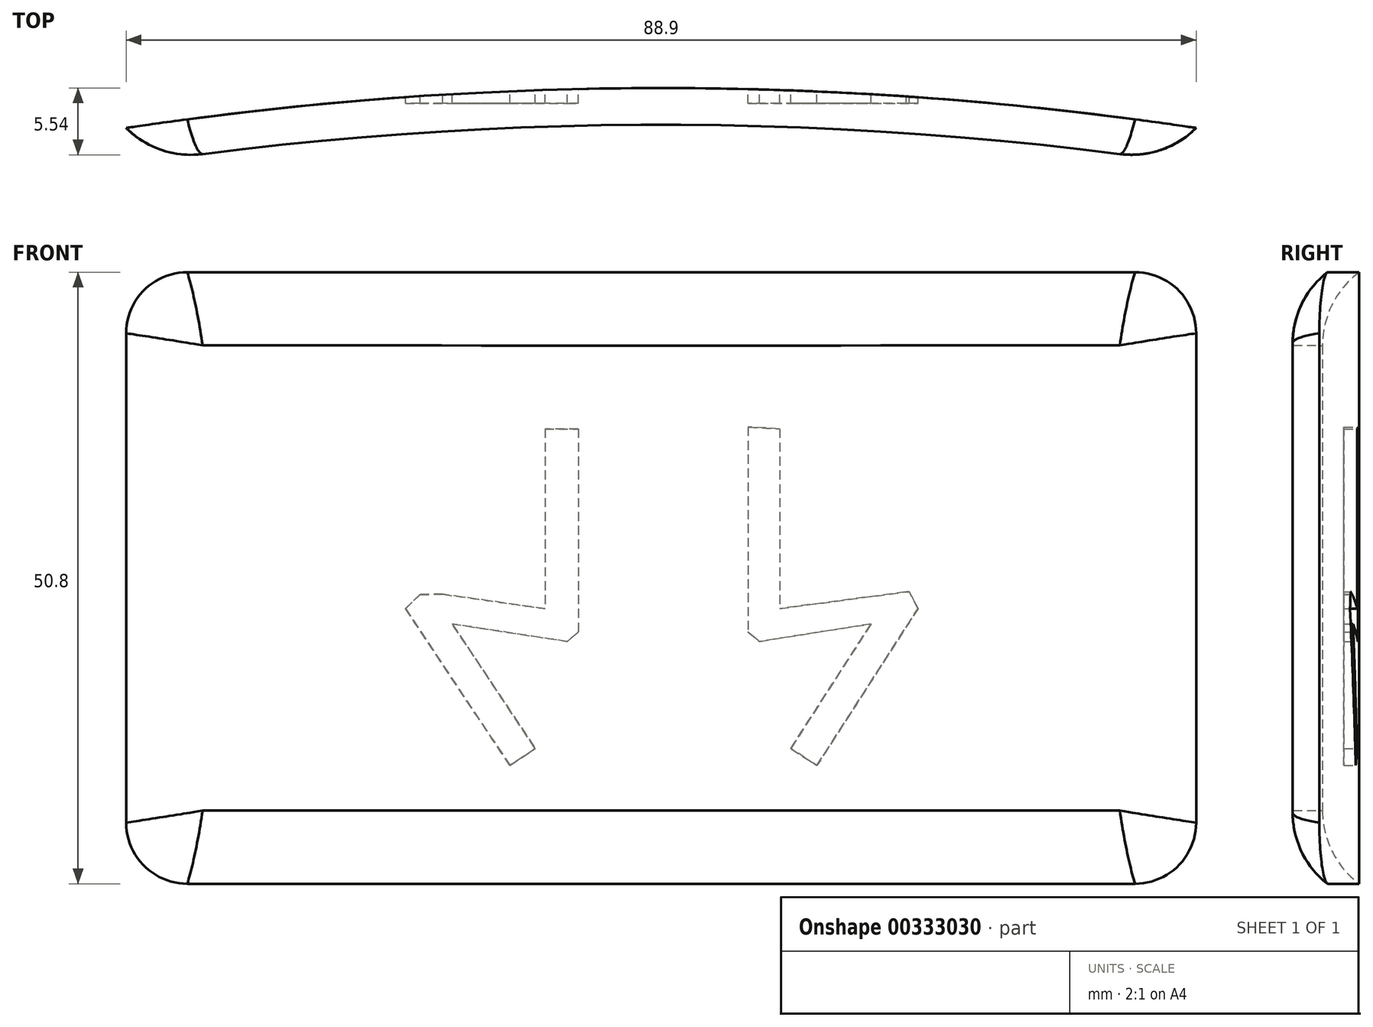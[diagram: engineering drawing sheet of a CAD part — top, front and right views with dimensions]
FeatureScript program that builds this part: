
annotation { "Feature Type Name" : "Feature", "Feature Type Description" : "" }
export const myFeature = defineFeature(function(context is Context, id is Id, definition is map)
    precondition{}
    {
        {
            var Q0;
            Q0=qCreatedBy(makeId("Top.planeOp"),FACE);
            var sketch = newSketch(context, id + "F0", { "sketchPlane" : qUnion([Q0])});
            skLineSegment(sketch, "E0", {"start": v(-42.15, 0) * mm, "end": v(-42.15, 3.05) * mm});
            skLineSegment(sketch, "E1", {"start": v(46.75, 0) * mm, "end": v(46.75, 3.05) * mm});
            skArc(sketch, "E2", {"start": v(46.75, 3.05) * mm, "mid": v(2.3, 6.36) * mm, "end": v(-42.15, 3.05) * mm});
            skArc(sketch, "E3", {"start": v(46.75, 0) * mm, "mid": v(2.3, 3.31) * mm, "end": v(-42.15, 0) * mm});
            skSolve(sketch);
        }
        {
            var Q0;
            Q0 = qSketchRegion(id + "F0", true);
            extrude(context, id + "F1", {"entities" : qUnion([Q0]), "depth" : 50.8 * mm});
        }
        {
            var Q0;
            Q0=makeQuery(id+"F1.opExtrude","CAP_EDGE",EDGE,{"disambiguationData":[OSD([sQuery(id+"F0.wireOp",EDGE,"E0")])],"isStart":true});
            var Q1;
            Q1=makeQuery(id+"F1.opExtrude","CAP_EDGE",EDGE,{"disambiguationData":[OSD([sQuery(id+"F0.wireOp",EDGE,"E1")])],"isStart":true});
            var Q2;
            Q2=makeQuery(id+"F1.opExtrude","CAP_EDGE",EDGE,{"disambiguationData":[OSD([sQuery(id+"F0.wireOp",EDGE,"E1")])],"isStart":false});
            var Q3;
            Q3=makeQuery(id+"F1.opExtrude","CAP_EDGE",EDGE,{"disambiguationData":[OSD([sQuery(id+"F0.wireOp",EDGE,"E0")])],"isStart":false});
            fillet(context, id + "F2", {"entities" : qUnion([Q0, Q1, Q2, Q3]), "radius" : 5.08 * mm, "tangentPropagation" : true, "allowEdgeOverflow" : false});
        }
        {
            var Q0;
            Q0=makeQuery(id+"F1.opExtrude","SWEPT_FACE",FACE,{"disambiguationData":[OSD([sQuery(id+"F0.wireOp",EDGE,"ed1f61be-c009-4c42-bc88-0e2171d65392")])]});
            var Q1;
            Q1=makeQuery(id+"F1.opExtrude","SWEPT_FACE",FACE,{"disambiguationData":[OSD([sQuery(id+"F0.wireOp",EDGE,"E3")])]});
            fillet(context, id + "F3", {"entities" : qUnion([Q0, Q1]), "radius" : 7.62 * mm, "tangentPropagation" : true, "allowEdgeOverflow" : false});
        }
        {
            var Q0;
            Q0=qCreatedBy(makeId("Front.planeOp"),FACE);
            cPlane(context, id + "F4", {"entities" : qUnion([Q0]), "cplaneType" : CPlaneType.OFFSET, "offset" : 7.62 * mm, "oppositeDirection" : true, "width" : 152.4 * mm, "height" : 152.4 * mm});
        }
        {
            var Q0;
            Q0=qCreatedBy(id+"F4.planeOp",FACE);
            var sketch = newSketch(context, id + "F5", { "sketchPlane" : qUnion([Q0])});
            skPoint(sketch, "E4.startSnap0", {"position": v(25.93, 24) * mm});
            skLineSegment(sketch, "E5", {"start": v(9.53, 37.94) * mm, "end": v(9.53, 20.9) * mm});
            skLineSegment(sketch, "E6", {"start": v(9.53, 20.9) * mm, "end": v(10.45, 20.13) * mm});
            skLineSegment(sketch, "E7", {"start": v(10.45, 20.13) * mm, "end": v(19.74, 21.59) * mm});
            skLineSegment(sketch, "E8", {"start": v(19.74, 21.59) * mm, "end": v(13.06, 11.23) * mm});
            skLineSegment(sketch, "E9", {"start": v(13.06, 11.23) * mm, "end": v(15.24, 9.82) * mm});
            skLineSegment(sketch, "E10", {"start": v(15.24, 9.82) * mm, "end": v(23.63, 22.85) * mm});
            skLineSegment(sketch, "E11", {"start": v(23.63, 22.85) * mm, "end": v(22.88, 24.27) * mm});
            skLineSegment(sketch, "E12", {"start": v(22.88, 24.27) * mm, "end": v(12.14, 22.85) * mm});
            skLineSegment(sketch, "E13", {"start": v(12.14, 22.85) * mm, "end": v(12.14, 37.78) * mm});
            skLineSegment(sketch, "E14", {"start": v(12.14, 37.78) * mm, "end": v(9.53, 37.94) * mm});
            skLineSegment(sketch, "E15", {"start": v(-4.6, 37.78) * mm, "end": v(-7.36, 37.78) * mm});
            skLineSegment(sketch, "E16", {"start": v(-7.36, 37.78) * mm, "end": v(-7.36, 22.85) * mm});
            skLineSegment(sketch, "E17", {"start": v(-7.36, 22.85) * mm, "end": v(-17.49, 24.27) * mm});
            skLineSegment(sketch, "E18", {"start": v(-17.49, 24.27) * mm, "end": v(-18.94, 22.85) * mm});
            skLineSegment(sketch, "E19", {"start": v(-18.94, 22.85) * mm, "end": v(-10.27, 9.82) * mm});
            skLineSegment(sketch, "E20", {"start": v(-10.27, 9.82) * mm, "end": v(-8.16, 11.23) * mm});
            skLineSegment(sketch, "E21", {"start": v(-8.16, 11.23) * mm, "end": v(-15.06, 21.59) * mm});
            skLineSegment(sketch, "E22", {"start": v(-15.06, 21.59) * mm, "end": v(-5.51, 20.13) * mm});
            skLineSegment(sketch, "E23", {"start": v(-5.51, 20.13) * mm, "end": v(-4.6, 20.9) * mm});
            skLineSegment(sketch, "E24", {"start": v(-4.6, 20.9) * mm, "end": v(-4.6, 37.78) * mm});
            skLineSegment(sketch, "E25", {"start": v(22.9, 24.25) * mm, "end": v(22.65, 24.24) * mm});
            skPoint(sketch, "E25.endSnap0", {"position": v(-21.25, 24) * mm});
            skLineSegment(sketch, "E26", {"start": v(28.56, 22.85) * mm, "end": v(28.56, 24.27) * mm});
            skPoint(sketch, "E27.end.orphan", {"position": v(-24.09, 22.85) * mm});
            skPoint(sketch, "E27.start.orphan", {"position": v(-24.09, 24) * mm});
            skLineSegment(sketch, "E28.trimOffspring", {"start": v(-15.85, 24.04) * mm, "end": v(-17.73, 24.03) * mm});
            skSolve(sketch);
        }
        {
            var Q0;
            Q0=makeQuery(id+"F5.imprint","IMPRINT",FACE,{"disambiguationData":[TD([[makeQuery(id+"F5.imprint","IMPRINT",EDGE,{"derivedFrom":sQuery(id+"F5.wireOp",EDGE,"E15")}),1.0]])]});
            var Q1;
            Q1=makeQuery(id+"F5.imprint","IMPRINT",FACE,{"disambiguationData":[TD([[makeQuery(id+"F5.imprint","IMPRINT",EDGE,{"derivedFrom":sQuery(id+"F5.wireOp",EDGE,"E5")}),1.0]])]});
            extrude(context, id + "F6", {"entities" : qUnion([Q0, Q1]), "operationType" : NewBodyOperationType.REMOVE, "depth" : 2.54 * mm});
        }
    });
